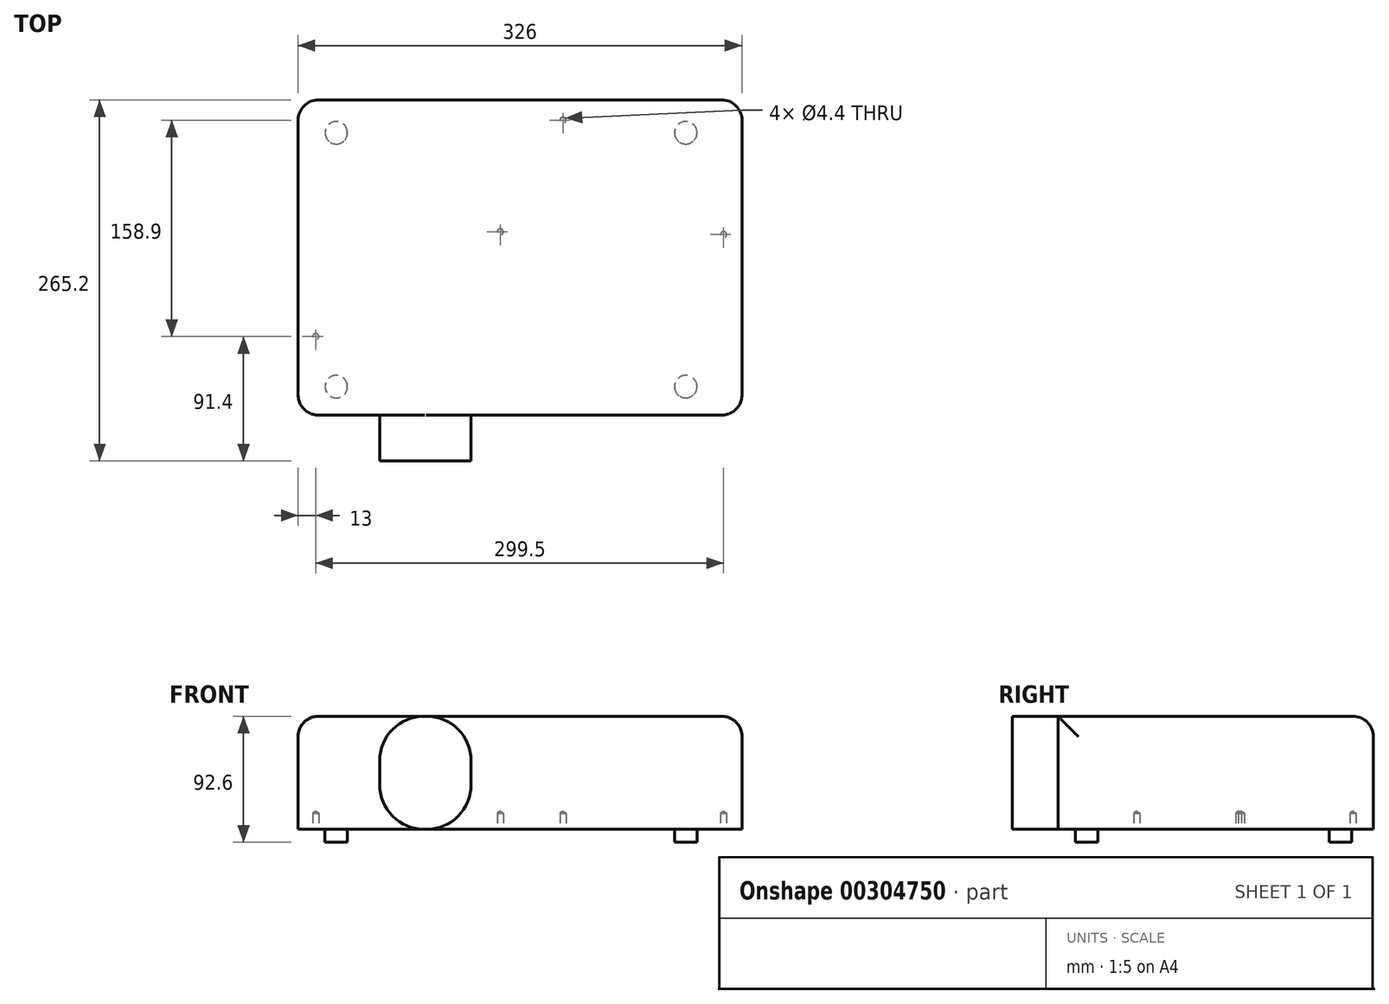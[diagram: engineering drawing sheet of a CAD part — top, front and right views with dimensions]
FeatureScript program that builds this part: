
annotation { "Feature Type Name" : "Feature", "Feature Type Description" : "" }
export const myFeature = defineFeature(function(context is Context, id is Id, definition is map)
    precondition{}
    {
        {
            var Q0;
            Q0=qCreatedBy(makeId("Top.planeOp"),FACE);
            var sketch = newSketch(context, id + "F0", { "sketchPlane" : qUnion([Q0])});
            skPoint(sketch, "E0.middle", {"position": v(0, 0) * mm});
            skLineSegment(sketch, "E1", {"start": v(0, -109.7) * mm, "end": v(0, 121.9) * mm, "construction": true});
            skLineSegment(sketch, "E2", {"start": v(-114.08, 0) * mm, "end": v(241, 0) * mm, "construction": true});
            skLineSegment(sketch, "E3", {"start": v(-93.5, 121.9) * mm, "end": v(-93.5, -109.7) * mm});
            skLineSegment(sketch, "E4", {"start": v(-93.5, -109.7) * mm, "end": v(-33.6, -109.7) * mm});
            skLineSegment(sketch, "E5", {"start": v(232.5, -109.7) * mm, "end": v(232.5, 121.9) * mm});
            skLineSegment(sketch, "E6", {"start": v(232.5, 121.9) * mm, "end": v(-93.5, 121.9) * mm});
            skPoint(sketch, "E7.orphan", {"position": v(0, -70.03) * mm});
            skLineSegment(sketch, "E8.bottom", {"start": v(-33.6, -143.3) * mm, "end": v(33.6, -143.3) * mm});
            skLineSegment(sketch, "E8.left", {"start": v(-33.6, -143.3) * mm, "end": v(-33.6, -109.7) * mm});
            skLineSegment(sketch, "E8.right", {"start": v(33.6, -143.3) * mm, "end": v(33.6, -109.7) * mm});
            skLineSegment(sketch, "E9.trimOffspring", {"start": v(33.6, -109.7) * mm, "end": v(232.5, -109.7) * mm});
            skSolve(sketch);
        }
        {
            var Q0;
            Q0=makeQuery(id+"F0.imprint","IMPRINT",FACE,{"disambiguationData":[TD([[makeQuery(id+"F0.imprint","IMPRINT",EDGE,{"derivedFrom":sQuery(id+"F0.wireOp",EDGE,"E3")}),1.0]])]});
            extrude(context, id + "F1", {"entities" : qUnion([Q0]), "depth" : (40.8 + 42.3) * mm});
        }
        {
            var Q0;
            Q0=makeQuery(id+"F1.opExtrude","CAP_FACE",FACE,{"disambiguationData":[OSD([sQuery(id+"F0.wireOp",EDGE,"E3"),sQuery(id+"F0.wireOp",EDGE,"E4"),sQuery(id+"F0.wireOp",EDGE,"E5"),sQuery(id+"F0.wireOp",EDGE,"E6"),sQuery(id+"F0.wireOp",EDGE,"E8.bottom"),sQuery(id+"F0.wireOp",EDGE,"E8.left"),sQuery(id+"F0.wireOp",EDGE,"E8.right"),sQuery(id+"F0.wireOp",EDGE,"E9.trimOffspring")])],"isStart":true});
            var sketch = newSketch(context, id + "F2", { "sketchPlane" : qUnion([Q0])});
            skCircle(sketch, "E10", {"center": v(-65.44, 88.73) * mm, "radius": 8.27 * mm});
            skCircle(sketch, "E11.0.1.0", {"center": v(-65.44, -97.76) * mm, "radius": 8.27 * mm});
            skCircle(sketch, "E11.1.0.0", {"center": v(191.17, 88.73) * mm, "radius": 8.27 * mm});
            skCircle(sketch, "E11.1.1.0", {"center": v(191.17, -97.76) * mm, "radius": 8.27 * mm});
            skLineSegment(sketch, "E11.direction1", {"start": v(-65.44, 88.73) * mm, "end": v(191.17, 88.73) * mm, "construction": true});
            skLineSegment(sketch, "E11.direction2", {"start": v(-65.44, 88.73) * mm, "end": v(-65.44, -97.76) * mm, "construction": true});
            skSolve(sketch);
        }
        {
            var Q0;
            Q0=qSketchRegion(id+"F2",true);
            extrude(context, id + "F3", {"entities" : qUnion([Q0]), "operationType" : NewBodyOperationType.ADD, "depth" : 9.5 * mm});
        }
        {
            var Q0;
            Q0=makeQuery(id+"F1.opExtrude","SWEPT_EDGE",EDGE,{"disambiguationData":[OSD([sQuery(id+"F0.wireOp",EDGE,"E3"),sQuery(id+"F0.wireOp",EDGE,"E4")])]});
            var Q1;
            Q1=makeQuery(id+"F1.opExtrude","SWEPT_EDGE",EDGE,{"disambiguationData":[OSD([sQuery(id+"F0.wireOp",EDGE,"E5"),sQuery(id+"F0.wireOp",EDGE,"E9.trimOffspring")])]});
            var Q2;
            Q2=makeQuery(id+"F1.opExtrude","SWEPT_EDGE",EDGE,{"disambiguationData":[OSD([sQuery(id+"F0.wireOp",EDGE,"E3"),sQuery(id+"F0.wireOp",EDGE,"E6")])]});
            var Q3;
            Q3=makeQuery(id+"F1.opExtrude","SWEPT_EDGE",EDGE,{"disambiguationData":[OSD([sQuery(id+"F0.wireOp",EDGE,"E5"),sQuery(id+"F0.wireOp",EDGE,"E6")])]});
            var Q4;
            Q4=makeQuery(id+"F1.opExtrude","CAP_EDGE",EDGE,{"disambiguationData":[OSD([sQuery(id+"F0.wireOp",EDGE,"E6")])],"isStart":false});
            var Q5;
            Q5=makeQuery(id+"F1.opExtrude","CAP_EDGE",EDGE,{"disambiguationData":[OSD([sQuery(id+"F0.wireOp",EDGE,"E3")])],"isStart":false});
            var Q6;
            Q6=makeQuery(id+"F1.opExtrude","CAP_EDGE",EDGE,{"disambiguationData":[OSD([sQuery(id+"F0.wireOp",EDGE,"E5")])],"isStart":false});
            fillet(context, id + "F4", {"entities" : qUnion([Q0, Q1, Q2, Q3, Q4, Q5, Q6]), "radius" : 15 * mm, "tangentPropagation" : true, "allowEdgeOverflow" : false});
        }
        {
            var Q0;
            Q0=makeQuery(id+"F1.opExtrude","CAP_EDGE",EDGE,{"disambiguationData":[OSD([sQuery(id+"F0.wireOp",EDGE,"E8.left")])],"isStart":false});
            var Q1;
            Q1=makeQuery(id+"F1.opExtrude","CAP_EDGE",EDGE,{"disambiguationData":[OSD([sQuery(id+"F0.wireOp",EDGE,"E8.right")])],"isStart":false});
            var Q2;
            Q2=makeQuery(id+"F1.opExtrude","CAP_EDGE",EDGE,{"disambiguationData":[OSD([sQuery(id+"F0.wireOp",EDGE,"E8.left")])],"isStart":true});
            var Q3;
            Q3=makeQuery(id+"F1.opExtrude","CAP_EDGE",EDGE,{"disambiguationData":[OSD([sQuery(id+"F0.wireOp",EDGE,"E8.right")])],"isStart":true});
            fillet(context, id + "F5", {"entities" : qUnion([Q0, Q1, Q2, Q3]), "radius" : 33 * mm, "tangentPropagation" : true, "allowEdgeOverflow" : false});
        }
        {
            var Q0;
            Q0=makeQuery(id+"F1.opExtrude","CAP_FACE",FACE,{"disambiguationData":[OSD([sQuery(id+"F0.wireOp",EDGE,"E3"),sQuery(id+"F0.wireOp",EDGE,"E4"),sQuery(id+"F0.wireOp",EDGE,"E5"),sQuery(id+"F0.wireOp",EDGE,"E6"),sQuery(id+"F0.wireOp",EDGE,"E8.bottom"),sQuery(id+"F0.wireOp",EDGE,"E8.left"),sQuery(id+"F0.wireOp",EDGE,"E8.right"),sQuery(id+"F0.wireOp",EDGE,"E9.trimOffspring")])],"isStart":true});
            var sketch = newSketch(context, id + "F6", { "sketchPlane" : qUnion([Q0])});
            skPoint(sketch, "E12", {"position": v(55, -25) * mm});
            skPoint(sketch, "E13", {"position": v(-80.5, 51.9) * mm});
            skPoint(sketch, "E14", {"position": v(101, -107) * mm});
            skPoint(sketch, "E15", {"position": v(219, -23) * mm});
            skSolve(sketch);
        }
        {
            var Q0;
            Q0=sQuery(id+"F6.wireOp",VERTEX,"E13");
            var Q1;
            Q1=sQuery(id+"F6.wireOp",VERTEX,"E12");
            var Q2;
            Q2=sQuery(id+"F6.wireOp",VERTEX,"E14");
            var Q3;
            Q3=sQuery(id+"F6.wireOp",VERTEX,"E15");
            var Q4;
            Q4=makeQuery(id+"F1.opExtrude","SWEPT_BODY",BODY,{"disambiguationData":[OSD([sQuery(id+"F0.wireOp",EDGE,"E3"),sQuery(id+"F0.wireOp",EDGE,"E4"),sQuery(id+"F0.wireOp",EDGE,"E5"),sQuery(id+"F0.wireOp",EDGE,"E6"),sQuery(id+"F0.wireOp",EDGE,"E8.bottom"),sQuery(id+"F0.wireOp",EDGE,"E8.left"),sQuery(id+"F0.wireOp",EDGE,"E8.right"),sQuery(id+"F0.wireOp",EDGE,"E9.trimOffspring")])]});
            hole(context, id + "F7", {"style" : HoleStyle.SIMPLE, "endStyle" : HoleEndStyle.BLIND, "standardTappedOrClearance" : lookupTablePath({ "standard" : "ISO", "fit" : "Normal", "size" : "M4", "type" : "Clearance" }), "standardBlindInLast" : lookupTablePath({ "fit" : "Standard", "standard" : "ISO", "size" : "M4", "type" : "Clearance" }), "holeDiameter" : 4.4 * mm, "holeDepth" : 12 * mm, "locations" : qUnion([Q0, Q1, Q2, Q3]), "scope" : qUnion([Q4])});
        }
    });
